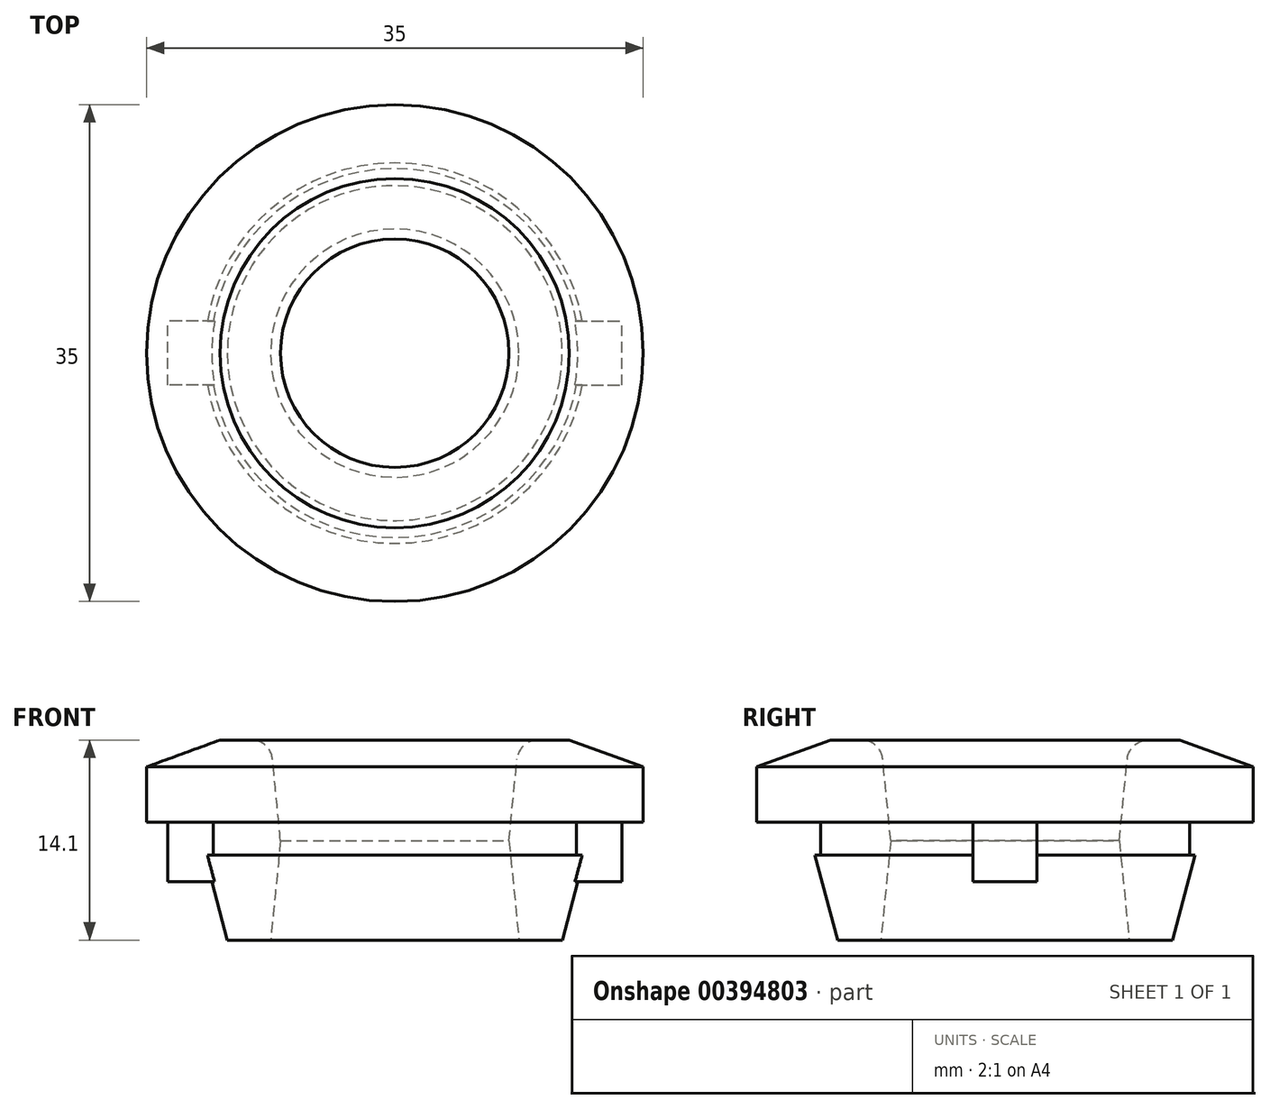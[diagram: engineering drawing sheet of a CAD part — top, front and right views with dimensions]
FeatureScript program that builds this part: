
annotation { "Feature Type Name" : "Feature", "Feature Type Description" : "" }
export const myFeature = defineFeature(function(context is Context, id is Id, definition is map)
    precondition{}
    {
        {
            var Q0;
            Q0=qCreatedBy(makeId("Front.planeOp"),FACE);
            var sketch = newSketch(context, id + "F0", { "sketchPlane" : qUnion([Q0])});
            skLineSegment(sketch, "E0", {"start": v(-8.75, 0) * mm, "end": v(-11.8, 0) * mm});
            skLineSegment(sketch, "E1", {"start": v(-11.8, 0) * mm, "end": v(-13.4, 6) * mm});
            skLineSegment(sketch, "E2", {"start": v(-13.4, 6) * mm, "end": v(-13, 6) * mm});
            skLineSegment(sketch, "E3", {"start": v(-13, 6) * mm, "end": v(-13, 8.3) * mm});
            skLineSegment(sketch, "E4", {"start": v(-13, 8.3) * mm, "end": v(-17.5, 8.3) * mm});
            skLineSegment(sketch, "E5", {"start": v(-17.5, 8.3) * mm, "end": v(-17.5, 12.2) * mm});
            skLineSegment(sketch, "E6", {"start": v(-17.5, 12.2) * mm, "end": v(-12.3, 14.1) * mm});
            skLineSegment(sketch, "E7", {"start": v(-12.3, 14.1) * mm, "end": v(-8.75, 14.1) * mm});
            skLineSegment(sketch, "E8", {"start": v(-8.75, 14.1) * mm, "end": v(-8.05, 7) * mm});
            skLineSegment(sketch, "E9", {"start": v(-8.05, 7) * mm, "end": v(-8.75, 0) * mm});
            skPoint(sketch, "E10.orphan", {"position": v(0, 0) * mm});
            skLineSegment(sketch, "E11", {"start": v(0, 0) * mm, "end": v(0, 15.5) * mm, "construction": true});
            skSolve(sketch);
        }
        {
            var Q0;
            Q0=makeQuery(id+"F0.imprint","IMPRINT",FACE,{"disambiguationData":[TD([[makeQuery(id+"F0.imprint","IMPRINT",EDGE,{"derivedFrom":sQuery(id+"F0.wireOp",EDGE,"E0")}),-1.0]])]});
            var Q1;
            Q1=sQuery(id+"F0.wireOp",EDGE,"E11");
            revolve(context, id + "F1", {"entities" : qUnion([Q0]), "axis" : qUnion([Q1]), "revolveType" : RevolveType.FULL});
        }
        {
            var Q0;
            Q0=makeQuery(id+"F1.opRevolve","SWEPT_EDGE",EDGE,{"disambiguationData":[OSD([sQuery(id+"F0.wireOp",EDGE,"E7"),sQuery(id+"F0.wireOp",EDGE,"E8")])]});
            fillet(context, id + "F2", {"entities" : qUnion([Q0]), "radius" : 1.5 * mm, "tangentPropagation" : true, "allowEdgeOverflow" : false});
        }
        {
            var Q0;
            Q0=makeQuery(id+"F1.opRevolve","SWEPT_FACE",FACE,{"disambiguationData":[OSD([sQuery(id+"F0.wireOp",EDGE,"E4")])]});
            var sketch = newSketch(context, id + "F3", { "sketchPlane" : qUnion([Q0])});
            skLineSegment(sketch, "E12.bottom", {"start": v(-12, 2.25) * mm, "end": v(-16, 2.25) * mm});
            skLineSegment(sketch, "E12.top", {"start": v(-12, -2.25) * mm, "end": v(-16, -2.25) * mm});
            skLineSegment(sketch, "E12.left", {"start": v(-12, 2.25) * mm, "end": v(-12, -2.25) * mm});
            skLineSegment(sketch, "E12.right", {"start": v(-16, 2.25) * mm, "end": v(-16, -2.25) * mm});
            skLineSegment(sketch, "E13", {"start": v(0, -18.14) * mm, "end": v(0, 19.06) * mm, "construction": true});
            skLineSegment(sketch, "E14.MirrorCS", {"start": v(12, 2.25) * mm, "end": v(16, 2.25) * mm});
            skLineSegment(sketch, "E15.MirrorCS", {"start": v(16, 2.25) * mm, "end": v(16, -2.25) * mm});
            skLineSegment(sketch, "E16.MirrorCS", {"start": v(12, -2.25) * mm, "end": v(16, -2.25) * mm});
            skLineSegment(sketch, "E17.MirrorCS", {"start": v(12, 2.25) * mm, "end": v(12, -2.25) * mm});
            skSolve(sketch);
        }
        {
            var Q0;
            {var subQ0=sQuery(id+"F3.wireOp",EDGE,"E12.right");Q0=makeQuery(id+"F3.imprint","IMPRINT",FACE,{"disambiguationData":[TD([[makeQuery(id+"F3.imprint","IMPRINT",EDGE,{"derivedFrom":subQ0}),1.0]])]});}
            var Q1;
            {var subQ0=sQuery(id+"F3.wireOp",EDGE,"E15.MirrorCS");Q1=makeQuery(id+"F3.imprint","IMPRINT",FACE,{"disambiguationData":[TD([[makeQuery(id+"F3.imprint","IMPRINT",EDGE,{"derivedFrom":subQ0}),-1.0]])]});}
            var Q2;
            {var subQ0=sQuery(id+"F3.wireOp",EDGE,"E17.MirrorCS");Q2=makeQuery(id+"F3.imprint","IMPRINT",FACE,{"disambiguationData":[TD([[makeQuery(id+"F3.imprint","IMPRINT",EDGE,{"derivedFrom":subQ0}),1.0]])]});}
            var Q3;
            {var subQ0=sQuery(id+"F3.wireOp",EDGE,"E12.left");Q3=makeQuery(id+"F3.imprint","IMPRINT",FACE,{"disambiguationData":[TD([[makeQuery(id+"F3.imprint","IMPRINT",EDGE,{"derivedFrom":subQ0}),-1.0]])]});}
            extrude(context, id + "F4", {"entities" : qUnion([Q0, Q1, Q2, Q3]), "operationType" : NewBodyOperationType.ADD, "depth" : 4.2 * mm});
        }
    });
